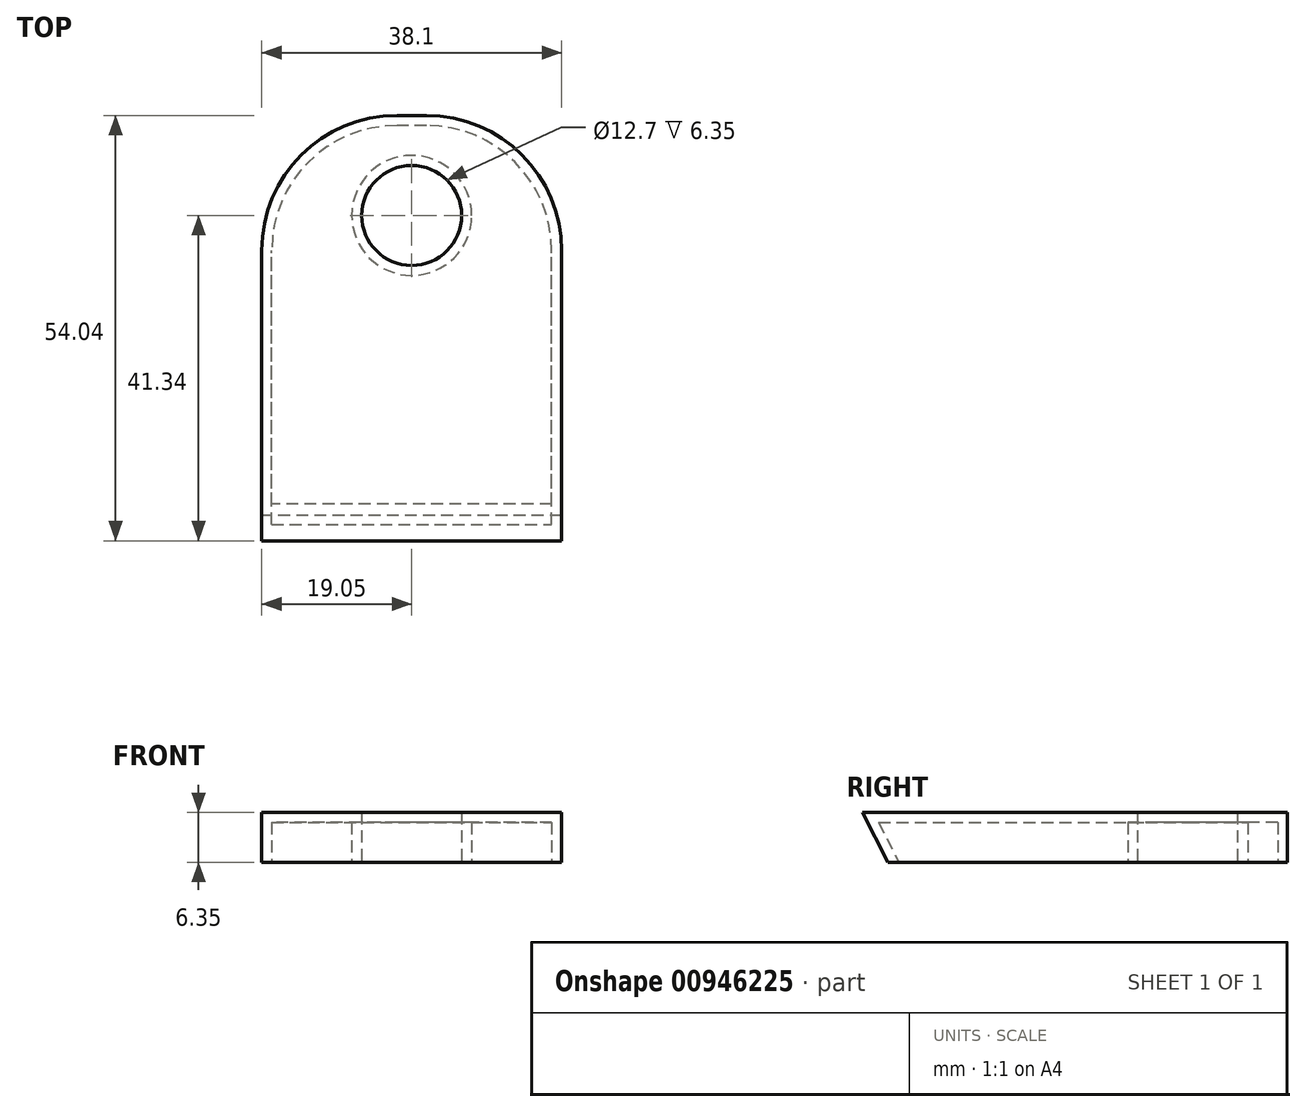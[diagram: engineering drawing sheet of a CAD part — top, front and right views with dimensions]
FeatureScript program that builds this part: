
annotation { "Feature Type Name" : "Feature", "Feature Type Description" : "" }
export const myFeature = defineFeature(function(context is Context, id is Id, definition is map)
    precondition{}
    {
        {
            var Q0;
            Q0=qCreatedBy(makeId("Top.planeOp"),FACE);
            var sketch = newSketch(context, id + "F0", { "sketchPlane" : qUnion([Q0])});
            skLineSegment(sketch, "E0.bottom", {"start": v(19.05, 0) * mm, "end": v(-19.05, 0) * mm});
            skLineSegment(sketch, "E0.top", {"start": v(19.05, 50.8) * mm, "end": v(-19.05, 50.8) * mm});
            skLineSegment(sketch, "E0.left", {"start": v(19.05, 0) * mm, "end": v(19.05, 50.8) * mm});
            skLineSegment(sketch, "E0.right", {"start": v(-19.05, 0) * mm, "end": v(-19.05, 50.8) * mm});
            skCircle(sketch, "E1", {"center": v(0, 38.1) * mm, "radius": 6.35 * mm});
            skSolve(sketch);
        }
        {
            var Q0;
            Q0 = qSketchRegion(id + "F0", true);
            extrude(context, id + "F1", {"entities" : qUnion([Q0]), "depth" : 6.35 * mm, "offsetDistance" : 25.4 * mm});
        }
        {
            var Q0;
            Q0=makeQuery(id+"F1.opExtrude","SWEPT_EDGE",EDGE,{"disambiguationData":[OSD([sQuery(id+"F0.wireOp",EDGE,"E0.top"),sQuery(id+"F0.wireOp",EDGE,"E0.right")])]});
            var Q1;
            Q1=makeQuery(id+"F1.opExtrude","SWEPT_EDGE",EDGE,{"disambiguationData":[OSD([sQuery(id+"F0.wireOp",EDGE,"E0.top"),sQuery(id+"F0.wireOp",EDGE,"E0.left")])]});
            fillet(context, id + "F2", {"entities" : qUnion([Q0, Q1]), "radius" : 17.17 * mm, "tangentPropagation" : true, "allowEdgeOverflow" : false});
        }
        {
            var Q0;
            Q0=makeQuery(id+"F1.opExtrude","SWEPT_FACE",FACE,{"disambiguationData":[OSD([sQuery(id+"F0.wireOp",EDGE,"E0.left")])]});
            var sketch = newSketch(context, id + "F3", { "sketchPlane" : qUnion([Q0])});
            skLineSegment(sketch, "E2", {"start": v(0, 6.35) * mm, "end": v(-3.24, 6.35) * mm});
            skLineSegment(sketch, "E3", {"start": v(-3.24, 6.35) * mm, "end": v(0, 0) * mm});
            skLineSegment(sketch, "E4", {"start": v(0, 0) * mm, "end": v(0, 6.35) * mm});
            skSolve(sketch);
        }
        {
            var Q0;
            Q0=makeQuery(id+"F3.imprint","IMPRINT",FACE,{"disambiguationData":[TD([[makeQuery(id+"F3.imprint","IMPRINT",EDGE,{"derivedFrom":sQuery(id+"F3.wireOp",EDGE,"E2")}),1.0]])]});
            extrude(context, id + "F4", {"entities" : qUnion([Q0]), "operationType" : NewBodyOperationType.ADD, "depth" : -38.1 * mm, "offsetDistance" : 25.4 * mm});
        }
        {
            var Q0;
            Q0=makeQuery(id+"F1.opExtrude","CAP_FACE",FACE,{"disambiguationData":[OSD([sQuery(id+"F0.wireOp",EDGE,"E0.bottom"),sQuery(id+"F0.wireOp",EDGE,"E0.top"),sQuery(id+"F0.wireOp",EDGE,"E0.left"),sQuery(id+"F0.wireOp",EDGE,"E0.right"),sQuery(id+"F0.wireOp",EDGE,"E1")])],"isStart":true});
            shell(context, id + "F5", {"entities" : qUnion([Q0]), "thickness" : 1.27 * mm});
        }
    });
